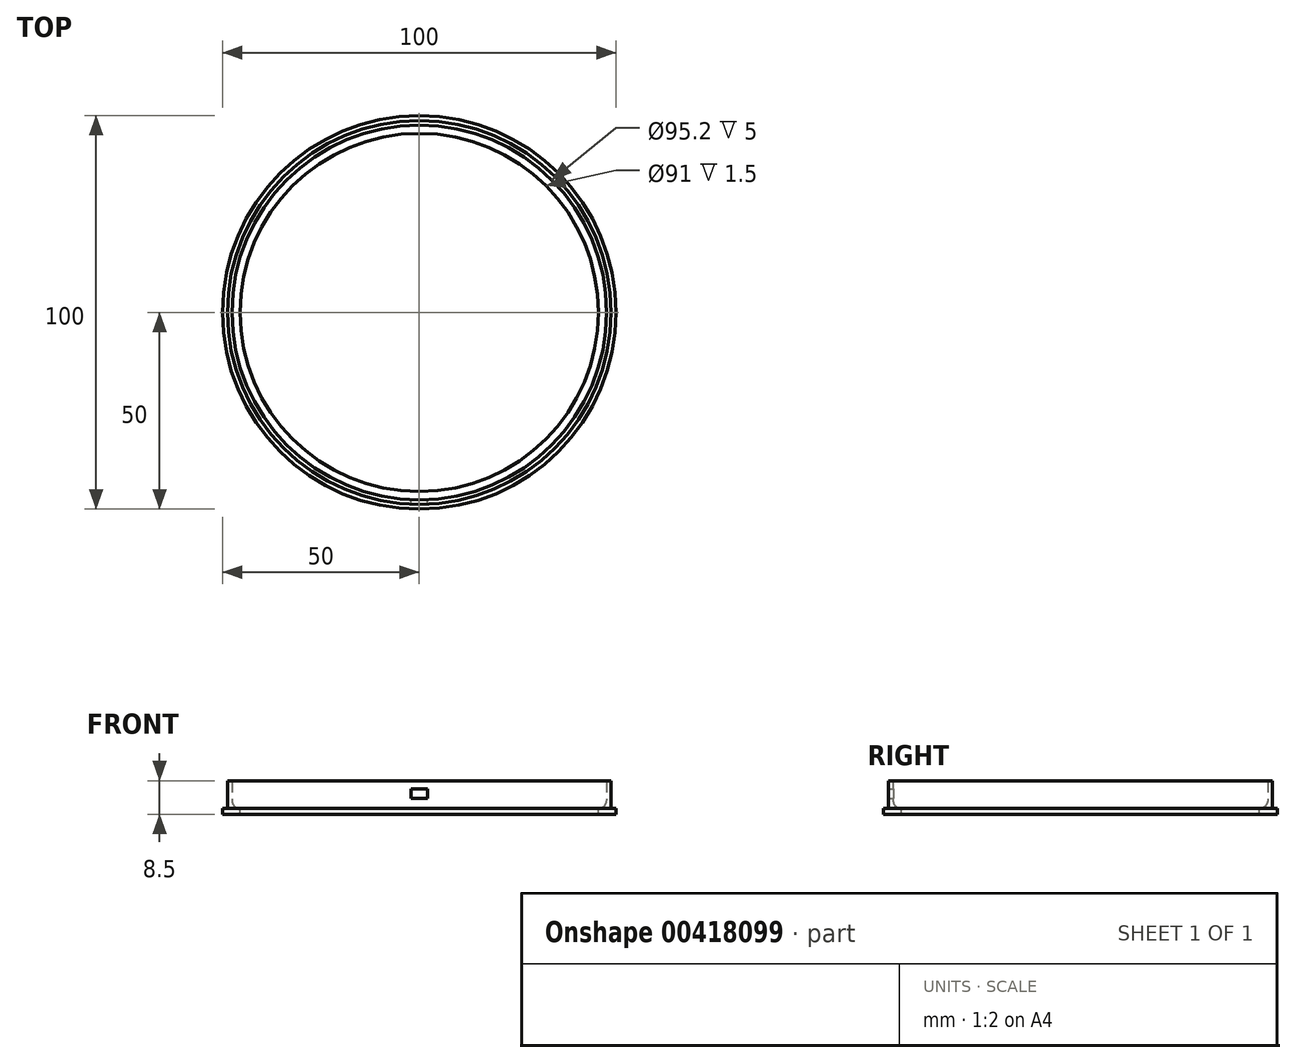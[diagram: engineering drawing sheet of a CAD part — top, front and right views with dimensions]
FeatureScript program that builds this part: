
annotation { "Feature Type Name" : "Feature", "Feature Type Description" : "" }
export const myFeature = defineFeature(function(context is Context, id is Id, definition is map)
    precondition{}
    {
        {
            var Q0;
            Q0=qCreatedBy(makeId("Top.planeOp"),FACE);
            var sketch = newSketch(context, id + "F0", { "sketchPlane" : qUnion([Q0])});
            skCircle(sketch, "E0", {"center": v(0, 0) * mm, "radius": 50 * mm});
            skSolve(sketch);
        }
        {
            var Q0;
            Q0=makeQuery(id+"F0.imprint","IMPRINT",FACE,{"disambiguationData":[TD([[makeQuery(id+"F0.imprint","IMPRINT",EDGE,{"derivedFrom":sQuery(id+"F0.wireOp",EDGE,"E0")}),1.0]])]});
            extrude(context, id + "F1", {"entities" : qUnion([Q0]), "depth" : 1.5 * mm});
        }
        {
            var Q0;
            Q0=makeQuery(id+"F1.opExtrude","CAP_FACE",FACE,{"disambiguationData":[OSD([sQuery(id+"F0.wireOp",EDGE,"E0")])],"isStart":false});
            var sketch = newSketch(context, id + "F2", { "sketchPlane" : qUnion([Q0])});
            skCircle(sketch, "E1", {"center": v(0, 0) * mm, "radius": 48.75 * mm});
            skCircle(sketch, "E2", {"center": v(0, 0) * mm, "radius": 47.6 * mm});
            skSolve(sketch);
        }
        {
            var Q0;
            Q0=makeQuery(id+"F2.imprint","IMPRINT",FACE,{"disambiguationData":[TD([[makeQuery(id+"F2.imprint","IMPRINT",EDGE,{"derivedFrom":sQuery(id+"F2.wireOp",EDGE,"E1")}),1.0]])]});
            extrude(context, id + "F3", {"entities" : qUnion([Q0]), "operationType" : NewBodyOperationType.ADD, "depth" : 7 * mm});
        }
        {
            var Q0;
            Q0=makeQuery(id+"F3.boolean.opBoolean","SPLIT",FACE,{"disambiguationData":[TD([makeQuery(id+"F3.opExtrude","SWEPT_FACE",FACE,{"disambiguationData":[OSD([sQuery(id+"F2.wireOp",EDGE,"E2")])]})])],"derivedFrom":makeQuery(id+"F1.opExtrude","CAP_FACE",FACE,{"disambiguationData":[OSD([sQuery(id+"F0.wireOp",EDGE,"E0")])],"isStart":false})});
            var sketch = newSketch(context, id + "F4", { "sketchPlane" : qUnion([Q0])});
            skCircle(sketch, "E3", {"center": v(0, 0) * mm, "radius": 45.5 * mm});
            skSolve(sketch);
        }
        {
            var Q0;
            Q0=makeQuery(id+"F4.imprint","IMPRINT",FACE,{"disambiguationData":[TD([[makeQuery(id+"F4.imprint","IMPRINT",EDGE,{"derivedFrom":sQuery(id+"F4.wireOp",EDGE,"E3")}),1.0]])]});
            extrude(context, id + "F5", {"entities" : qUnion([Q0]), "operationType" : NewBodyOperationType.REMOVE, "oppositeDirection" : true, "depth" : 25 * mm});
        }
        {
            var Q0;
            Q0=qCreatedBy(makeId("Front.planeOp"),FACE);
            var sketch = newSketch(context, id + "F6", { "sketchPlane" : qUnion([Q0])});
            skLineSegment(sketch, "E4.bottom", {"start": v(2.1, 4) * mm, "end": v(-2.1, 4) * mm});
            skLineSegment(sketch, "E4.top", {"start": v(2.1, 6.5) * mm, "end": v(-2.1, 6.5) * mm});
            skLineSegment(sketch, "E4.left", {"start": v(2.1, 4) * mm, "end": v(2.1, 6.5) * mm});
            skLineSegment(sketch, "E4.right", {"start": v(-2.1, 4) * mm, "end": v(-2.1, 6.5) * mm});
            skPoint(sketch, "E4.middle", {"position": v(0, 5.25) * mm});
            skSolve(sketch);
        }
        {
            var Q0;
            Q0=makeQuery(id+"F6.imprint","IMPRINT",FACE,{"disambiguationData":[TD([[makeQuery(id+"F6.imprint","IMPRINT",EDGE,{"derivedFrom":sQuery(id+"F6.wireOp",EDGE,"E4.bottom")}),-1.0]])]});
            extrude(context, id + "F7", {"entities" : qUnion([Q0]), "operationType" : NewBodyOperationType.REMOVE, "depth" : 150.9 * mm});
        }
        {
            var Q0;
            Q0=makeQuery(id+"F3.opExtrude","CAP_EDGE",EDGE,{"disambiguationData":[OSD([sQuery(id+"F2.wireOp",EDGE,"E2")])],"isStart":true});
            fillet(context, id + "F8", {"entities" : qUnion([Q0]), "radius" : 2 * mm, "tangentPropagation" : true, "allowEdgeOverflow" : false});
        }
    });
